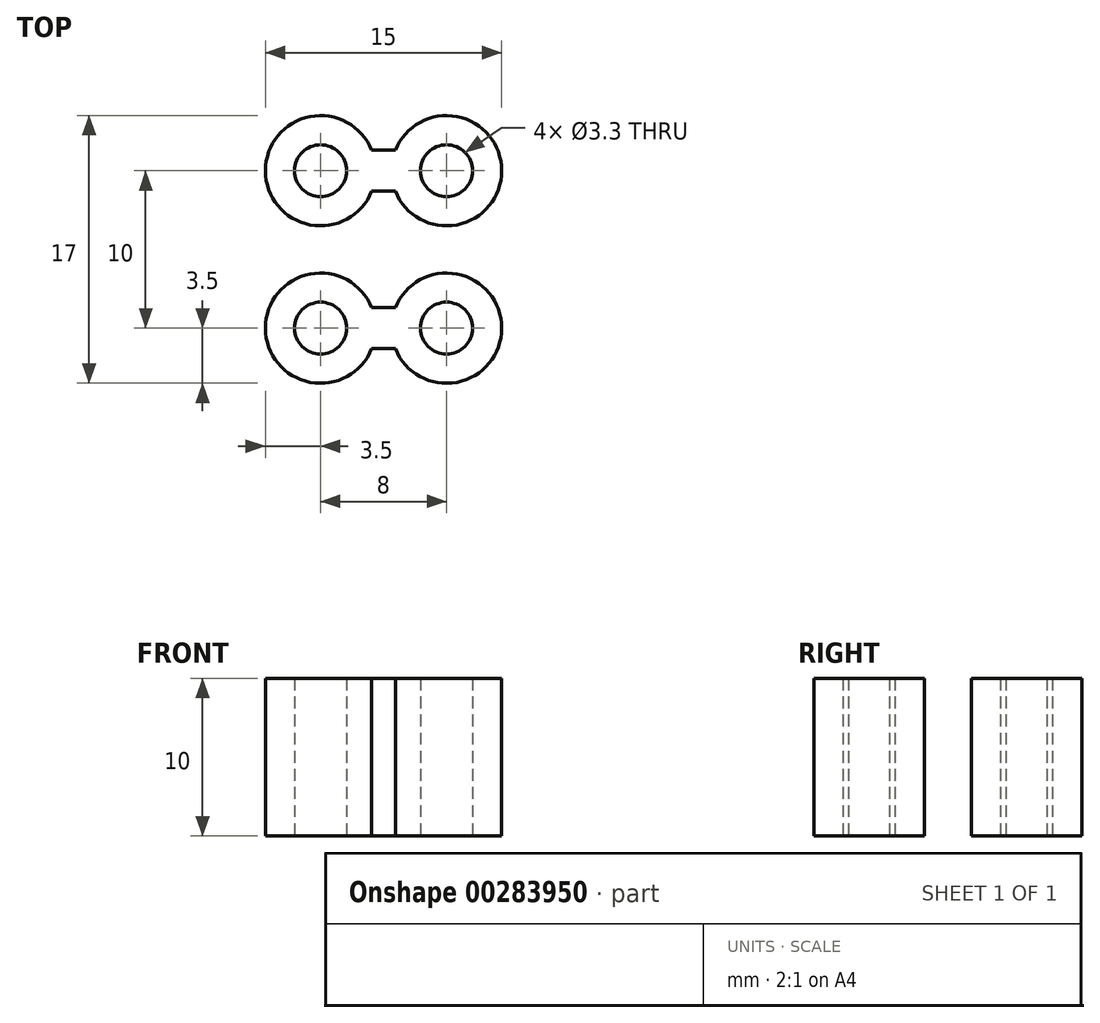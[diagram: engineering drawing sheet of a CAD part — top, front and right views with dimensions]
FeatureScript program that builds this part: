
annotation { "Feature Type Name" : "Feature", "Feature Type Description" : "" }
export const myFeature = defineFeature(function(context is Context, id is Id, definition is map)
    precondition{}
    {
        {
            var Q0;
            Q0=qCreatedBy(makeId("Top.planeOp"),FACE);
            var sketch = newSketch(context, id + "F0", { "sketchPlane" : qUnion([Q0])});
            skCircle(sketch, "E0", {"center": v(0, 0) * mm, "radius": 1.65 * mm});
            skCircle(sketch, "E1", {"center": v(8, 0) * mm, "radius": 1.65 * mm});
            skArc(sketch, "E2", {"start": v(3.25, 1.3) * mm, "mid": v(-3.5, 0) * mm, "end": v(3.25, -1.3) * mm});
            skArc(sketch, "E3", {"start": v(4.75, -1.3) * mm, "mid": v(11.5, 0) * mm, "end": v(4.75, 1.3) * mm});
            skLineSegment(sketch, "E4", {"start": v(3.25, 1.3) * mm, "end": v(4.75, 1.3) * mm});
            skLineSegment(sketch, "E5", {"start": v(0, 0) * mm, "end": v(8, 0) * mm, "construction": true});
            skLineSegment(sketch, "E6.MirrorCS", {"start": v(3.25, -1.3) * mm, "end": v(4.75, -1.3) * mm});
            skSolve(sketch);
        }
        {
            var Q0;
            Q0 = qSketchRegion(id + "F0", true);
            extrude(context, id + "F1", {"entities" : qUnion([Q0]), "depth" : 10 * mm});
        }
        {
            var Q0;
            Q0=makeQuery(id+"F1.opExtrude","SWEPT_BODY",BODY,{"disambiguationData":[OSD([sQuery(id+"F0.wireOp",EDGE,"wT9ajSf1-VFyA-s0li-BS3e-45ltDH9Wu2vk"),sQuery(id+"F0.wireOp",EDGE,"XwVfz5V7-l2eV-bDCl-JNy5-aE0BYsH4Xz1K"),sQuery(id+"F0.wireOp",EDGE,"E0"),sQuery(id+"F0.wireOp",EDGE,"E1")])]});
            transform(context, id + "F2", {"entities" : qUnion([Q0]), "transformType" : TransformType.TRANSLATION_3D, "dx" : 0 * mm, "dy" : 10 * mm, "dz" : 0 * mm, "makeCopy" : true});
        }
    });
